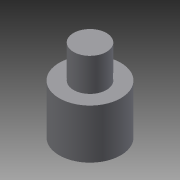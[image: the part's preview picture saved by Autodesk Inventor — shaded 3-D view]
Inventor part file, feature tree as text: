
AUTODESK INVENTOR PART (.ipt)
format: ipt  version: 2015 (Build 190159000, 159)  size: 90,624 bytes
history: native  units: mm
features: sketch x3, extrude x2, plane x1, hole x1
ambient origin geometry x8: Origin, YZ Plane, XZ Plane, XY Plane, X Axis, Y Axis, Z Axis, Center Point
bodies: Solid1 (feature_tree)
feature tree (7):
  extrude  "Extrusion1"  Depth=9.0mm TaperAngle=0.0deg
  plane  "Work Plane1"
  hole  "Hole1"  [1 undecoded]
  extrude  "Extrusion3"  Depth=6.0mm TaperAngle=0.0deg
  sketch  "Sketch1"  dims[d0=11.2mm d1=9.0mm d2=0.0mm]
  sketch  "Sketch3"  dims[d9=2.4mm]
  sketch  "Sketch4"  dims[d10=2.459mm d11=5.6mm d12=4.0mm d13=2.0mm d14=90.0deg d15=5.6mm d16=0.0mm d17=6.0mm d18=6.0mm d19=0.0mm]
note: 1 required parameter value undecoded (feature->parameter linkage not recoverable at this tier; creation-order binding heuristic only, values carry confidence <= 0.55)
